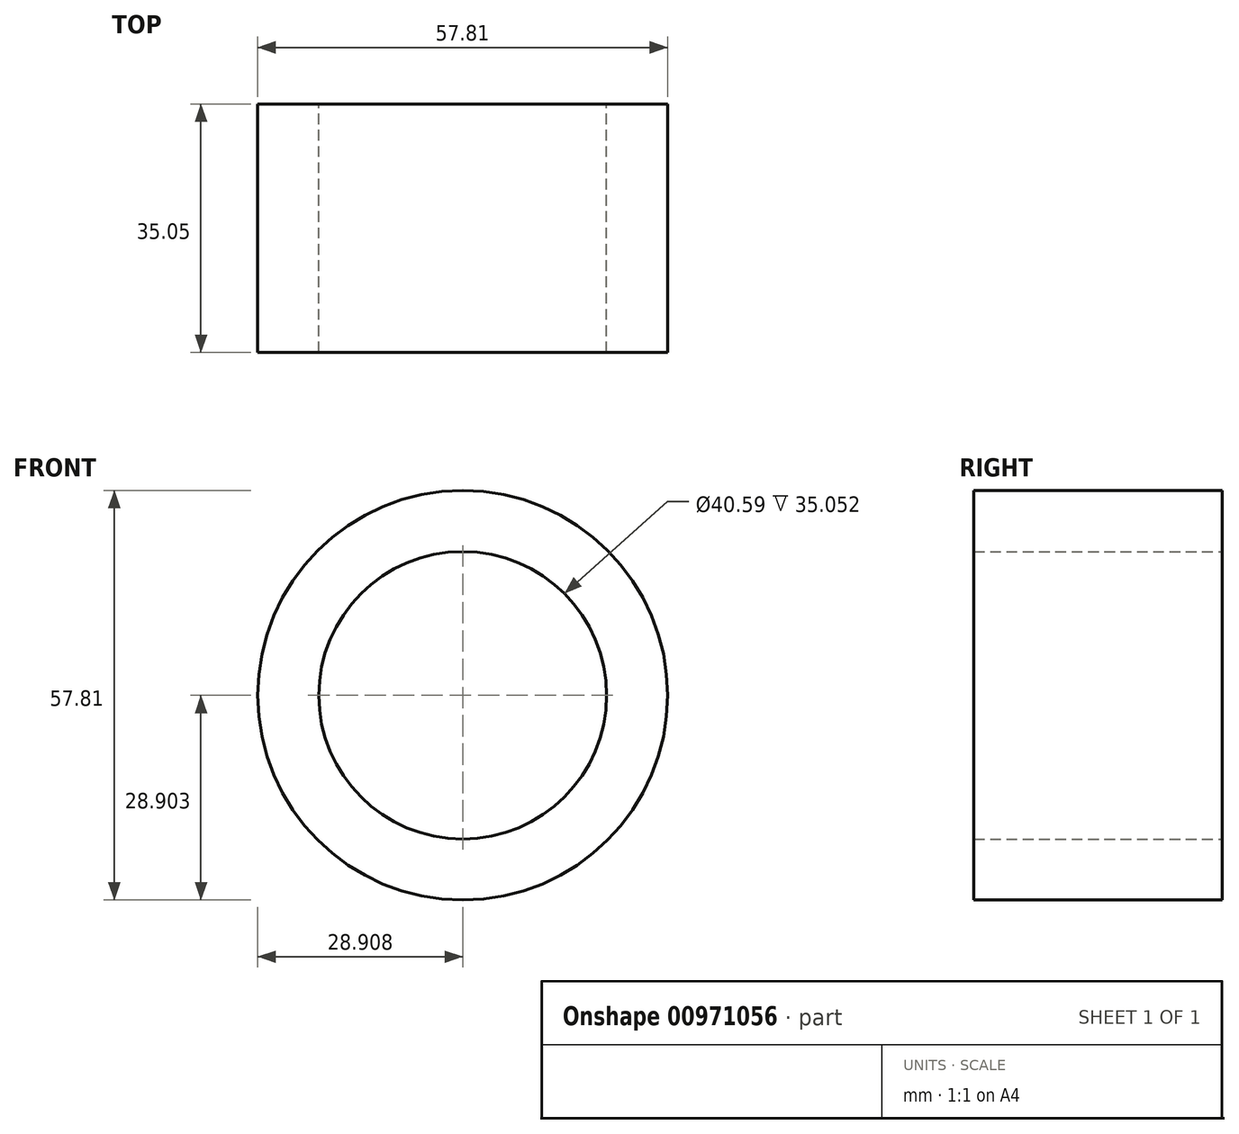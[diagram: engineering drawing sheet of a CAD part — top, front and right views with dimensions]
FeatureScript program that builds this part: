
annotation { "Feature Type Name" : "Feature", "Feature Type Description" : "" }
export const myFeature = defineFeature(function(context is Context, id is Id, definition is map)
    precondition{}
    {
        {
            var Q0;
            Q0=qCreatedBy(makeId("Front.planeOp"),FACE);
            var sketch = newSketch(context, id + "F0", { "sketchPlane" : qUnion([Q0])});
            skCircle(sketch, "E0", {"center": v(-77.13, -28.79) * mm, "radius": 28.9 * mm});
            skCircle(sketch, "E1", {"center": v(-77.13, -28.79) * mm, "radius": 20.3 * mm});
            skSolve(sketch);
        }
        {
            var Q0;
            Q0=makeQuery(id+"F0.imprint","IMPRINT",FACE,{"disambiguationData":[TD([[makeQuery(id+"F0.imprint","IMPRINT",EDGE,{"derivedFrom":sQuery(id+"F0.wireOp",EDGE,"E0")}),1.0]])]});
            extrude(context, id + "F1", {"entities" : qUnion([Q0]), "depth" : 35.05 * mm, "offsetDistance" : 25.4 * mm});
        }
    });
